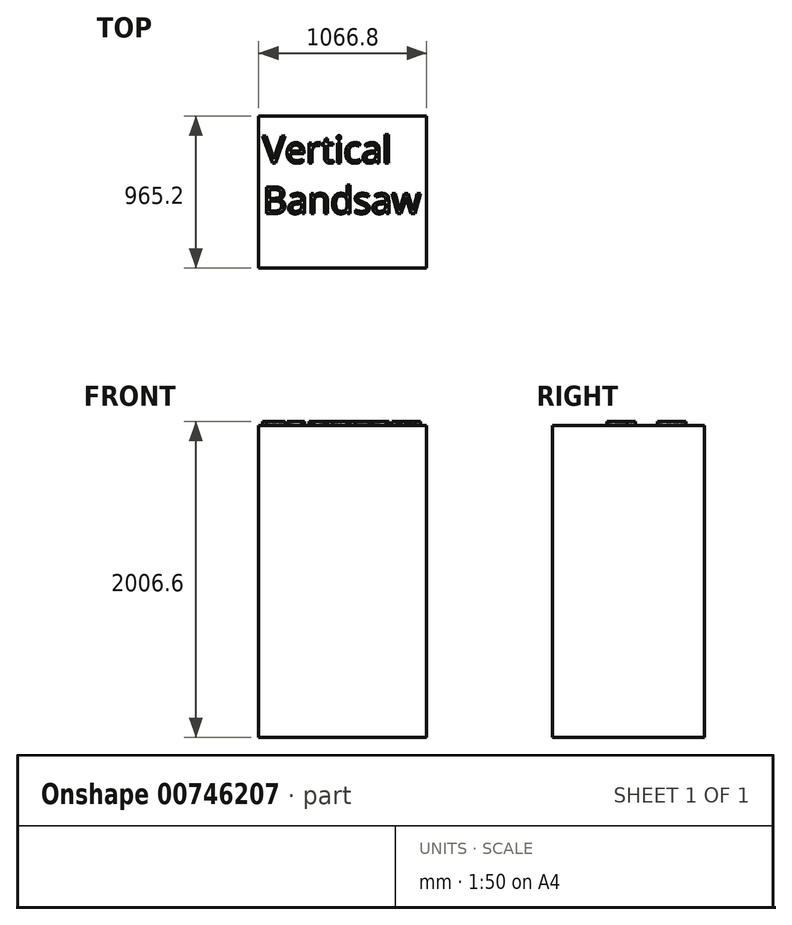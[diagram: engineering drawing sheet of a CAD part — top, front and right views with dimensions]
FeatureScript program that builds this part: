
annotation { "Feature Type Name" : "Feature", "Feature Type Description" : "" }
export const myFeature = defineFeature(function(context is Context, id is Id, definition is map)
    precondition{}
    {
        {
            var Q0;
            Q0=qCreatedBy(makeId("Top.planeOp"),FACE);
            var sketch = newSketch(context, id + "F0", { "sketchPlane" : qUnion([Q0])});
            skLineSegment(sketch, "E0.bottom", {"start": v(533.4, -482.6) * mm, "end": v(-533.4, -482.6) * mm});
            skLineSegment(sketch, "E0.top", {"start": v(533.4, 482.6) * mm, "end": v(-533.4, 482.6) * mm});
            skLineSegment(sketch, "E0.left", {"start": v(533.4, -482.6) * mm, "end": v(533.4, 482.6) * mm});
            skLineSegment(sketch, "E0.right", {"start": v(-533.4, -482.6) * mm, "end": v(-533.4, 482.6) * mm});
            skPoint(sketch, "E0.middle", {"position": v(0, 0) * mm});
            skSolve(sketch);
        }
        {
            var Q0;
            Q0 = qSketchRegion(id + "F0", true);
            extrude(context, id + "F1", {"entities" : qUnion([Q0]), "depth" : 1981.2 * mm, "offsetDistance" : 25.4 * mm});
        }
        {
            var Q0;
            Q0=makeQuery(id+"F1.opExtrude","CAP_FACE",FACE,{"disambiguationData":[OSD([sQuery(id+"F0.wireOp",EDGE,"E0.bottom"),sQuery(id+"F0.wireOp",EDGE,"E0.top"),sQuery(id+"F0.wireOp",EDGE,"E0.left"),sQuery(id+"F0.wireOp",EDGE,"E0.right")])],"isStart":false});
            var sketch = newSketch(context, id + "F2", { "sketchPlane" : qUnion([Q0])});
            skText(sketch, "E1", { "text": "Vertical \nBandsaw\n", "fontName": "OpenSans-Regular.ttf"});
            const initialGuessF2  = {"E1": [-0.508, 0.1853, 1, 0, 0.1703]};
            skSetInitialGuess(sketch, initialGuessF2);
            skSolve(sketch);
        }
        {
            var Q0;
            Q0 = qSketchRegion(id + "F2", true);
            extrude(context, id + "F3", {"entities" : qUnion([Q0]), "operationType" : NewBodyOperationType.ADD, "depth" : 25.4 * mm, "offsetDistance" : 25.4 * mm});
        }
    });
